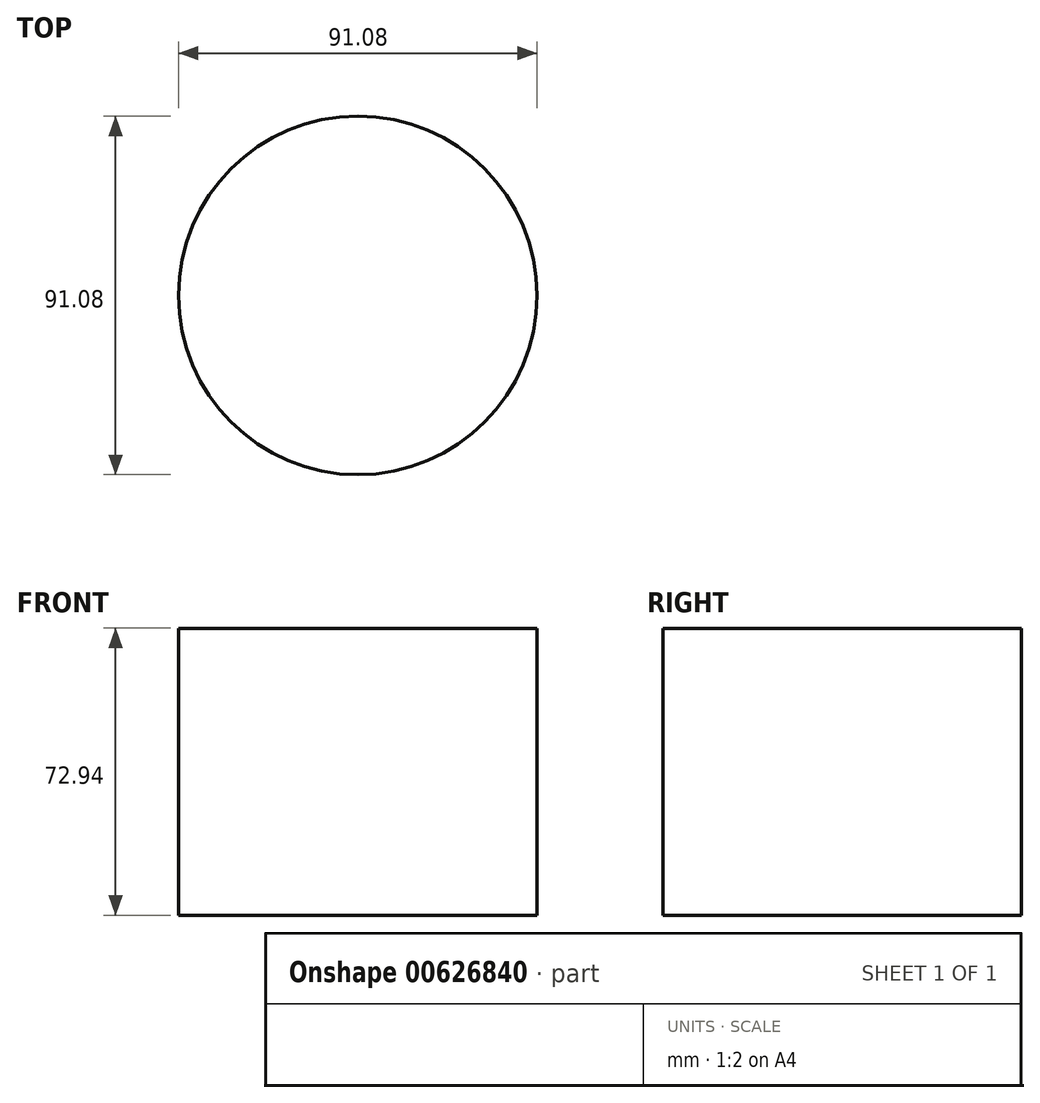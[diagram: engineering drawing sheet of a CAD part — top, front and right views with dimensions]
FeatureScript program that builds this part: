
annotation { "Feature Type Name" : "Feature", "Feature Type Description" : "" }
export const myFeature = defineFeature(function(context is Context, id is Id, definition is map)
    precondition{}
    {
        {
            var Q0;
            Q0=qCreatedBy(makeId("Top.planeOp"),FACE);
            var sketch = newSketch(context, id + "F0", { "sketchPlane" : qUnion([Q0])});
            skCircle(sketch, "E0", {"center": v(0, 0) * mm, "radius": 45.54 * mm});
            skSolve(sketch);
        }
        {
            var Q0;
            Q0=makeQuery(id+"F0.imprint","IMPRINT",FACE,{"disambiguationData":[TD([[makeQuery(id+"F0.imprint","IMPRINT",EDGE,{"derivedFrom":sQuery(id+"F0.wireOp",EDGE,"E0")}),1.0]])]});
            extrude(context, id + "F1", {"entities" : qUnion([Q0]), "depth" : 72.94 * mm, "offsetDistance" : 25.4 * mm});
        }
    });
